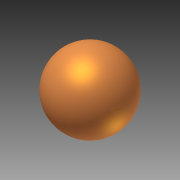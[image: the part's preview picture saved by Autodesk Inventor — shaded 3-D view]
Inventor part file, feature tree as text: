
AUTODESK INVENTOR PART (.ipt)
format: ipt  version: 2012 (Build 160160000, 160)  size: 100,864 bytes
history: native  units: in
note: dims shown in document units (in); Inventor stores cm internally (conversion verified against a paired STEP export)
features: revolve x1, sketch x1
ambient origin geometry x8: Origin, YZ Plane, XZ Plane, XY Plane, X Axis, Y Axis, Z Axis, Center Point
bodies: Solid1 (feature_tree)
feature tree (2):
  revolve  "Revolution1"  Angle=90.0deg
  sketch  "Sketch1"  dims[d0=7.5in d1=90.0deg]
